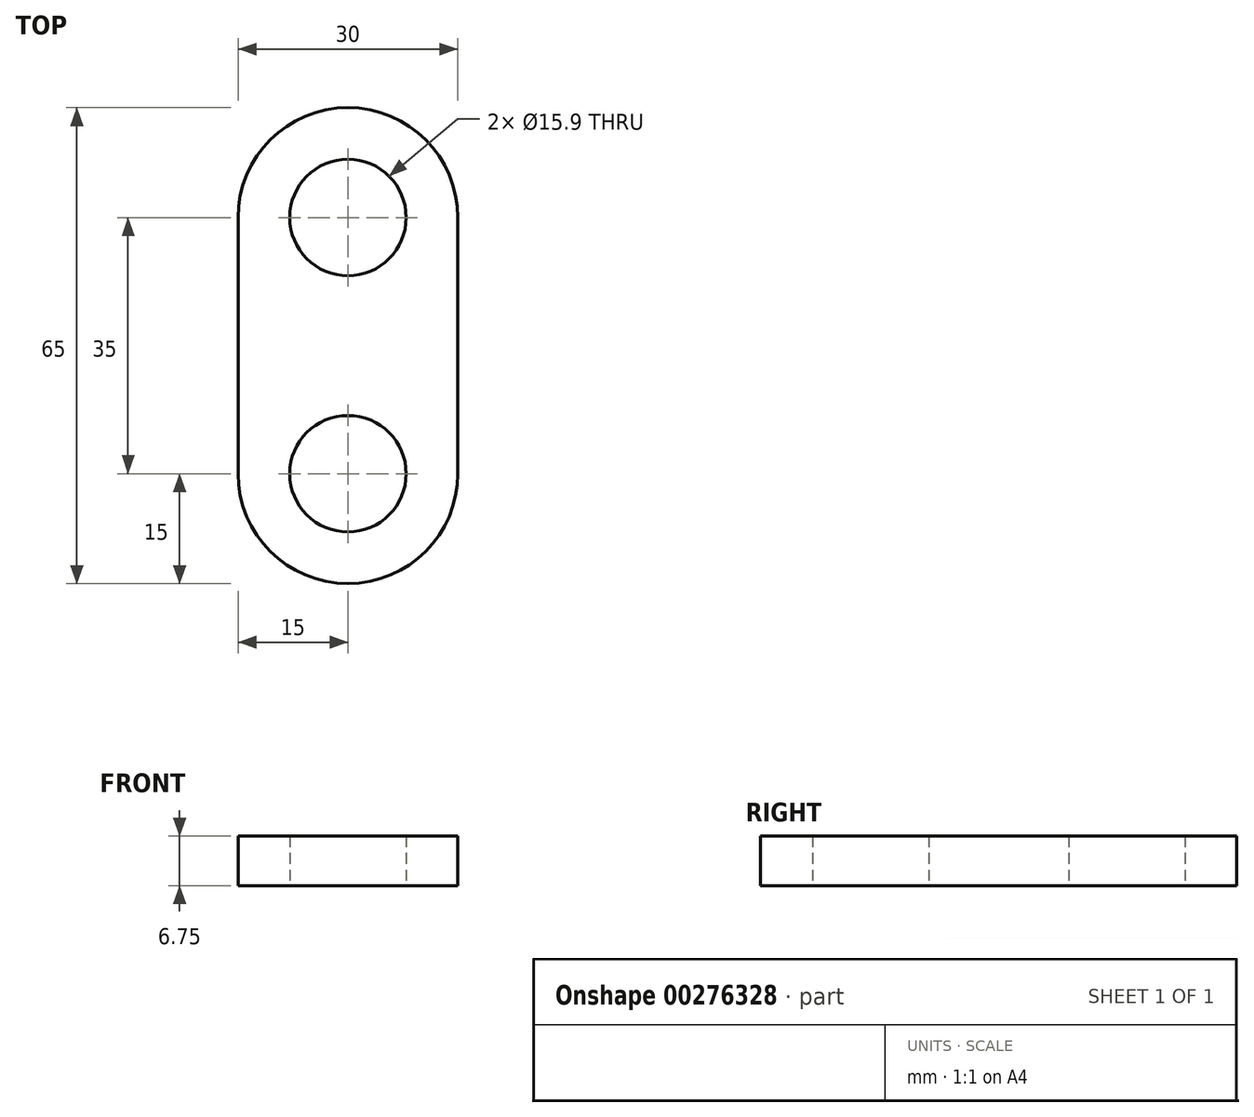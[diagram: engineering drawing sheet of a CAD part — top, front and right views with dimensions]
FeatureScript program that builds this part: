
annotation { "Feature Type Name" : "Feature", "Feature Type Description" : "" }
export const myFeature = defineFeature(function(context is Context, id is Id, definition is map)
    precondition{}
    {
        {
            var Q0;
            Q0=qCreatedBy(makeId("Top.planeOp"),FACE);
            var sketch = newSketch(context, id + "F0", { "sketchPlane" : qUnion([Q0])});
            skLineSegment(sketch, "E0.bottom", {"start": v(15, -17.5) * mm, "end": v(-15, -17.5) * mm, "construction": true});
            skLineSegment(sketch, "E0.top", {"start": v(15, 17.5) * mm, "end": v(-15, 17.5) * mm, "construction": true});
            skLineSegment(sketch, "E0.left", {"start": v(15, -17.5) * mm, "end": v(15, 17.5) * mm});
            skLineSegment(sketch, "E0.right", {"start": v(-15, -17.5) * mm, "end": v(-15, 17.5) * mm});
            skPoint(sketch, "E0.middle", {"position": v(0, 0) * mm});
            skArc(sketch, "E1", {"start": v(-15, 17.5) * mm, "mid": v(0, 32.5) * mm, "end": v(15, 17.5) * mm});
            skArc(sketch, "E2", {"start": v(15, -17.5) * mm, "mid": v(0, -32.5) * mm, "end": v(-15, -17.5) * mm});
            skCircle(sketch, "E3", {"center": v(0, 17.5) * mm, "radius": 7.95 * mm});
            skCircle(sketch, "E4", {"center": v(0, -17.5) * mm, "radius": 7.95 * mm});
            skSolve(sketch);
        }
        {
            var Q0;
            Q0=makeQuery(id+"F0.imprint","IMPRINT",FACE,{"disambiguationData":[TD([[makeQuery(id+"F0.imprint","IMPRINT",EDGE,{"derivedFrom":sQuery(id+"F0.wireOp",EDGE,"E0.left")}),1.0]])]});
            extrude(context, id + "F1", {"entities" : qUnion([Q0]), "depth" : 6.75 * mm});
        }
    });
